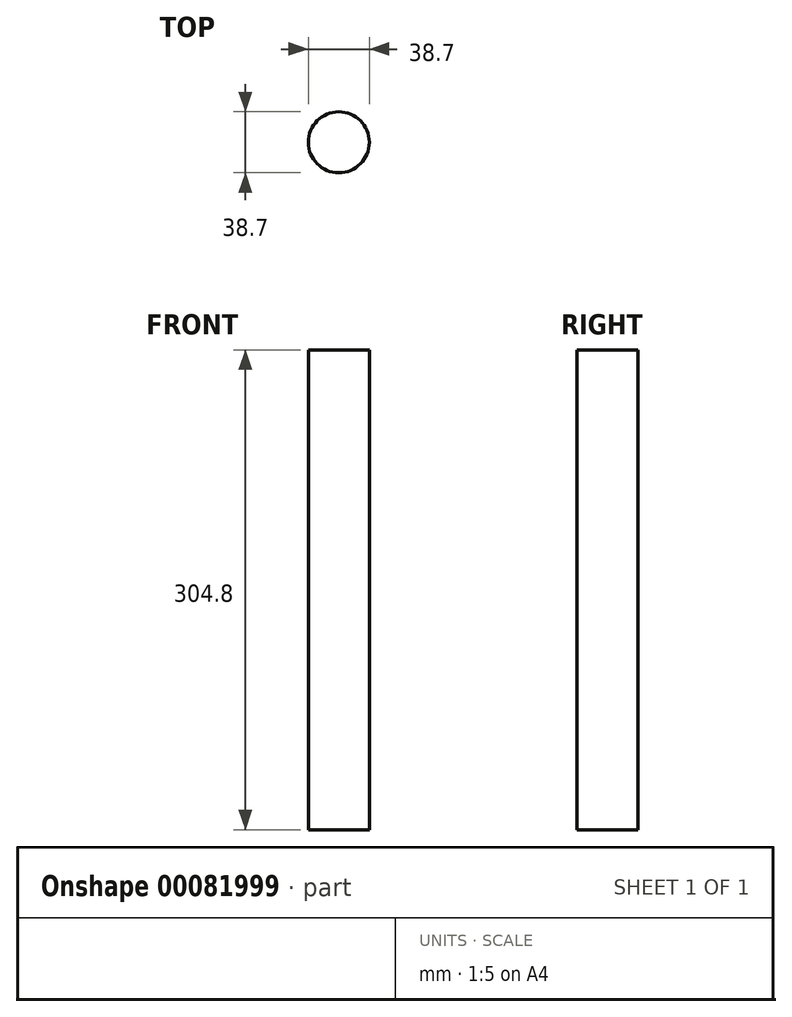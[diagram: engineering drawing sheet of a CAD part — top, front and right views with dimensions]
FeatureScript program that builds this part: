
annotation { "Feature Type Name" : "Feature", "Feature Type Description" : "" }
export const myFeature = defineFeature(function(context is Context, id is Id, definition is map)
    precondition{}
    {
        {
            var Q0;
            Q0=qCreatedBy(makeId("Top.planeOp"),FACE);
            var sketch = newSketch(context, id + "F0", { "sketchPlane" : qUnion([Q0])});
            skCircle(sketch, "E0", {"center": v(0, 0) * mm, "radius": 19.35 * mm});
            skSolve(sketch);
        }
        {
            var Q0;
            Q0=makeQuery(id+"F0.imprint","IMPRINT",FACE,{"disambiguationData":[TD([[makeQuery(id+"F0.imprint","IMPRINT",EDGE,{"derivedFrom":sQuery(id+"F0.wireOp",EDGE,"E0")}),1.0]])]});
            extrude(context, id + "F1", {"entities" : qUnion([Q0]), "depth" : 304.8 * mm});
        }
    });
